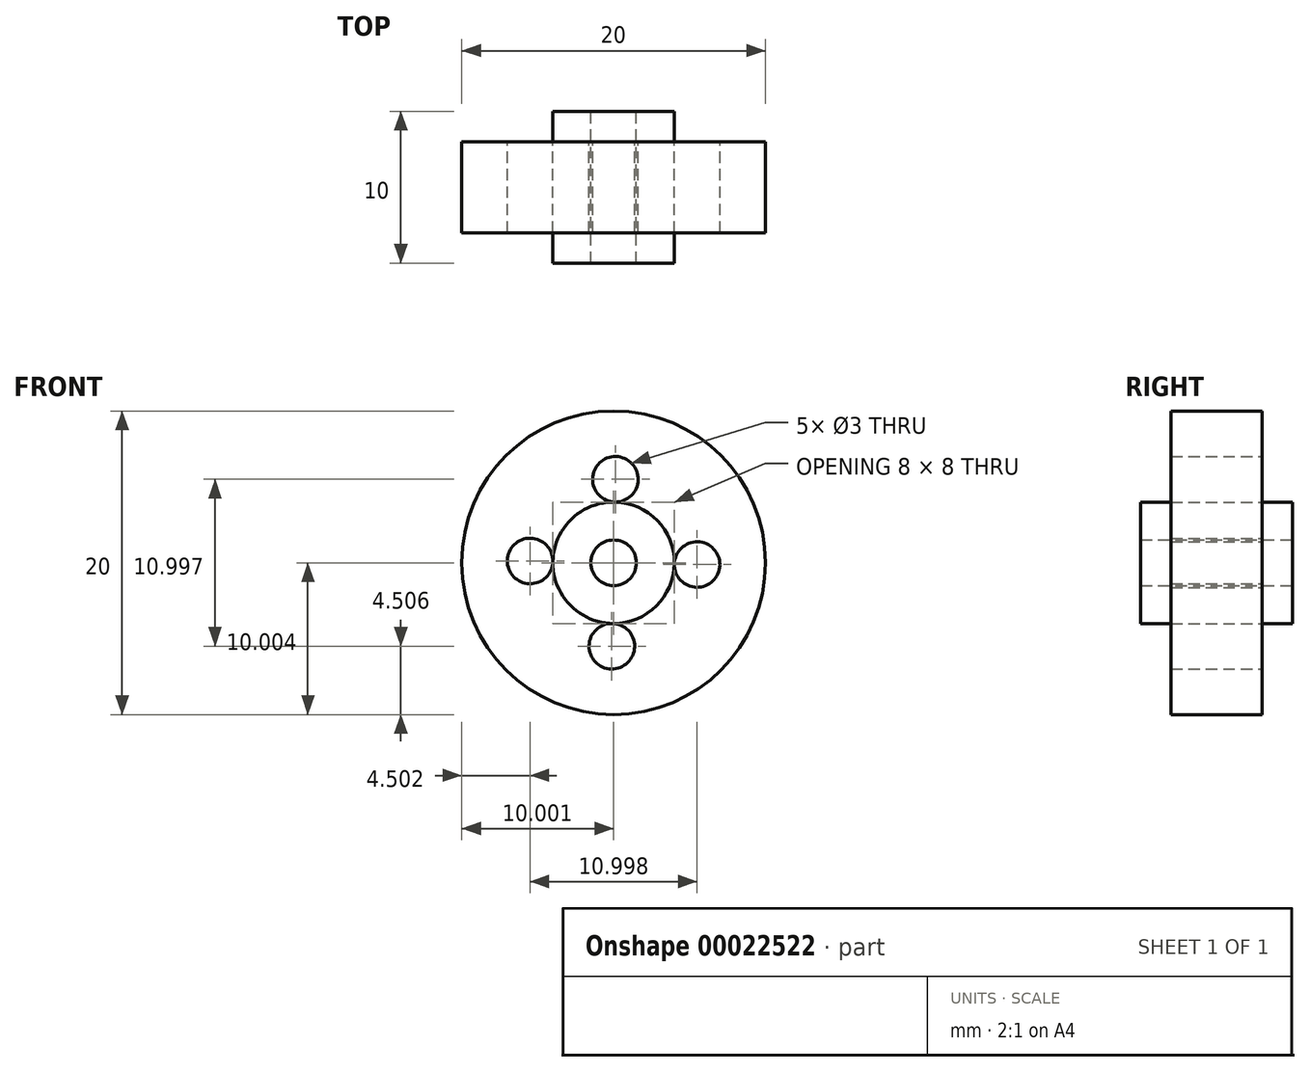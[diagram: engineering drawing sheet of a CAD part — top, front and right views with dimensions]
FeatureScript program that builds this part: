
annotation { "Feature Type Name" : "Feature", "Feature Type Description" : "" }
export const myFeature = defineFeature(function(context is Context, id is Id, definition is map)
    precondition{}
    {
        {
            var Q0;
            Q0=qCreatedBy(makeId("Front.planeOp"),FACE);
            var sketch = newSketch(context, id + "F0", { "sketchPlane" : qUnion([Q0])});
            skCircle(sketch, "E0", {"center": v(-55.8, 24.91) * mm, "radius": 10 * mm});
            skCircle(sketch, "E1", {"center": v(-55.8, 24.91) * mm, "radius": 4 * mm});
            skCircle(sketch, "E2", {"center": v(-55.8, 24.91) * mm, "radius": 1.5 * mm});
            skCircle(sketch, "E3", {"center": v(-55.68, 30.41) * mm, "radius": 1.5 * mm});
            skCircle(sketch, "E4.1.0", {"center": v(-61.3, 25.03) * mm, "radius": 1.5 * mm});
            skCircle(sketch, "E4.2.0", {"center": v(-55.92, 19.42) * mm, "radius": 1.5 * mm});
            skCircle(sketch, "E4.3.0", {"center": v(-50.3, 24.8) * mm, "radius": 1.5 * mm});
            skSolve(sketch);
        }
        {
            var Q0;
            Q0=makeQuery(id+"F0.imprint","IMPRINT",FACE,{"disambiguationData":[TD([[makeQuery(id+"F0.imprint","IMPRINT",EDGE,{"derivedFrom":sQuery(id+"F0.wireOp",EDGE,"E0")}),1.0]])]});
            var Q1;
            Q1=makeQuery(id+"F0.imprint","IMPRINT",FACE,{"disambiguationData":[TD([[makeQuery(id+"F0.imprint","IMPRINT",EDGE,{"derivedFrom":sQuery(id+"F0.wireOp",EDGE,"E2")}),-1.0]])]});
            extrude(context, id + "F1", {"entities" : qUnion([Q0, Q1]), "depth" : 6 * mm});
        }
        {
            var Q0;
            Q0=makeQuery(id+"F0.imprint","IMPRINT",FACE,{"disambiguationData":[TD([[makeQuery(id+"F0.imprint","IMPRINT",EDGE,{"derivedFrom":sQuery(id+"F0.wireOp",EDGE,"E2")}),-1.0]])]});
            extrude(context, id + "F2", {"entities" : qUnion([Q0]), "operationType" : NewBodyOperationType.ADD, "oppositeDirection" : true, "depth" : 2 * mm});
        }
        {
            var Q0;
            Q0=makeQuery(id+"F0.imprint","IMPRINT",FACE,{"disambiguationData":[TD([[makeQuery(id+"F0.imprint","IMPRINT",EDGE,{"derivedFrom":sQuery(id+"F0.wireOp",EDGE,"E2")}),-1.0]])]});
            extrude(context, id + "F3", {"entities" : qUnion([Q0]), "operationType" : NewBodyOperationType.ADD, "depth" : 8 * mm});
        }
    });
